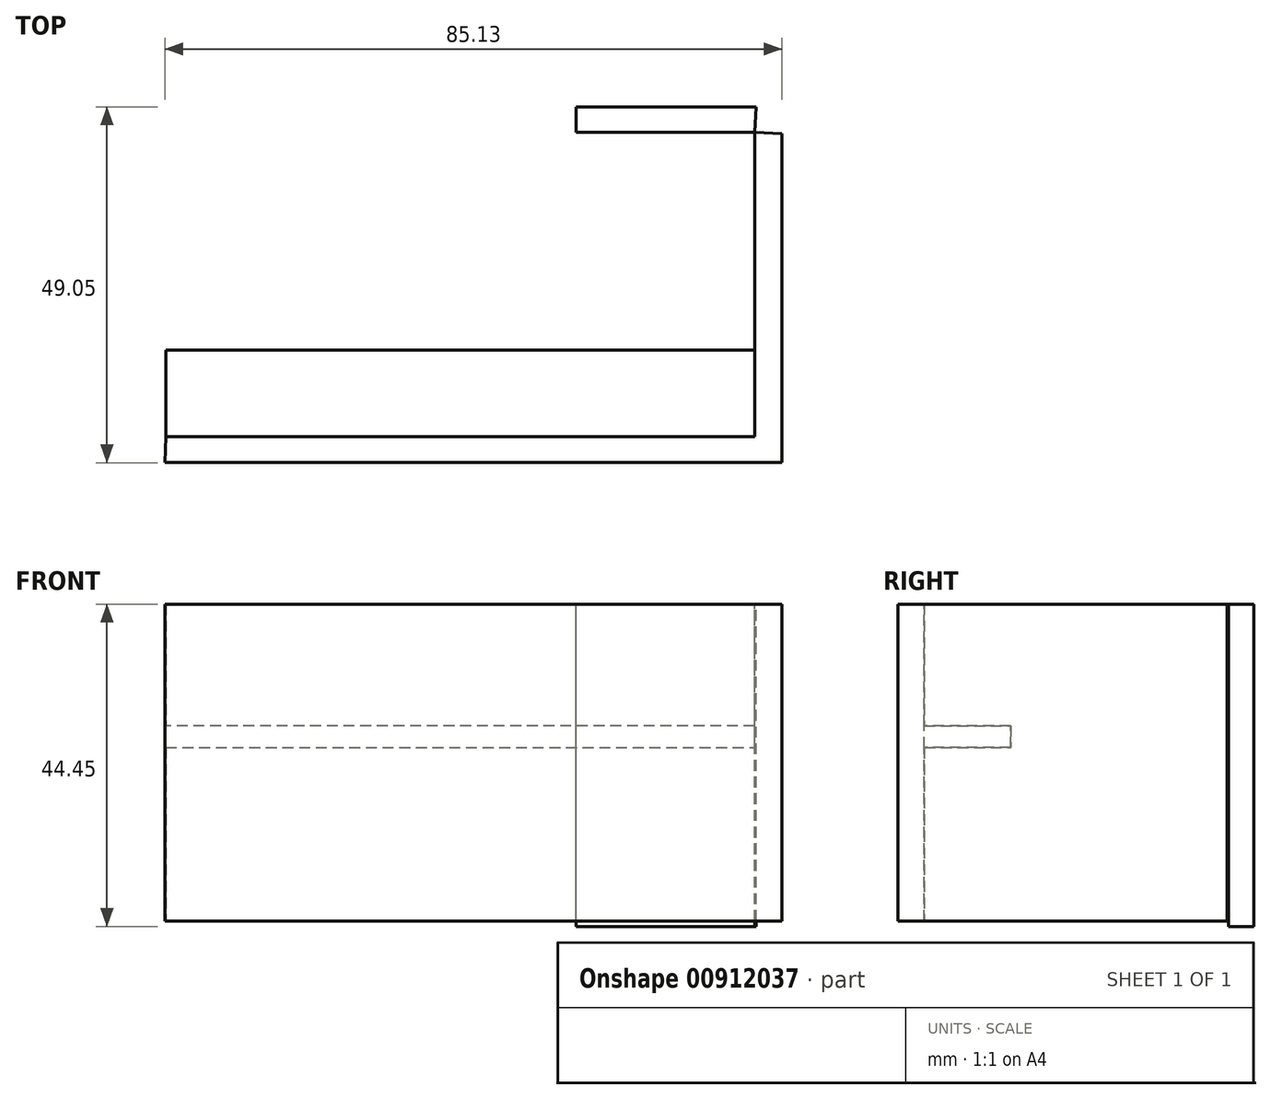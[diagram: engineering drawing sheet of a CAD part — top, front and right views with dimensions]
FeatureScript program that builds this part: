
annotation { "Feature Type Name" : "Feature", "Feature Type Description" : "" }
export const myFeature = defineFeature(function(context is Context, id is Id, definition is map)
    precondition{}
    {
        {
            var Q0;
            Q0=qCreatedBy(makeId("Top.planeOp"),FACE);
            var sketch = newSketch(context, id + "F0", { "sketchPlane" : qUnion([Q0])});
            skLineSegment(sketch, "E0", {"start": v(-39.37, -23.5) * mm, "end": v(41.83, -23.5) * mm});
            skLineSegment(sketch, "E1", {"start": v(41.83, -23.5) * mm, "end": v(41.83, 18.49) * mm});
            skLineSegment(sketch, "E2", {"start": v(41.83, 18.49) * mm, "end": v(-39.37, 18.49) * mm});
            skLineSegment(sketch, "E3", {"start": v(-39.37, 18.49) * mm, "end": v(-39.37, -23.5) * mm});
            skLineSegment(sketch, "E4", {"start": v(41.83, 10.61) * mm, "end": v(17.22, 10.61) * mm});
            skLineSegment(sketch, "E5", {"start": v(17.22, 10.61) * mm, "end": v(17.22, 18.49) * mm});
            skLineSegment(sketch, "E6", {"start": v(-39.37, 3.32) * mm, "end": v(-47.74, 3.32) * mm});
            skLineSegment(sketch, "E7", {"start": v(-47.74, 3.32) * mm, "end": v(-47.74, 29.92) * mm});
            skLineSegment(sketch, "E8", {"start": v(-47.74, 29.92) * mm, "end": v(-10, 29.92) * mm});
            skLineSegment(sketch, "E9", {"start": v(-10, 29.92) * mm, "end": v(-10, 18.49) * mm});
            skLineSegment(sketch, "E10", {"start": v(17.2, 15.15) * mm, "end": v(17.2, 21.95) * mm});
            skLineSegment(sketch, "E11", {"start": v(-10.12, 15.15) * mm, "end": v(-10, 22.18) * mm});
            skLineSegment(sketch, "E12", {"start": v(12.97, -27.73) * mm, "end": v(12.97, -18.71) * mm});
            skLineSegment(sketch, "E13", {"start": v(-9.3, -27.09) * mm, "end": v(-9.3, -18.07) * mm});
            skLineSegment(sketch, "E14", {"start": v(-39.37, -11.56) * mm, "end": v(-47.98, -11.56) * mm});
            skLineSegment(sketch, "E15", {"start": v(-47.98, -11.56) * mm, "end": v(-47.98, -22.58) * mm});
            skLineSegment(sketch, "E16", {"start": v(-39.37, -22.49) * mm, "end": v(-47.98, -22.58) * mm});
            skLineSegment(sketch, "E17", {"start": v(17.2, 21.95) * mm, "end": v(42.03, 21.95) * mm});
            skLineSegment(sketch, "E18", {"start": v(41.83, 18.49) * mm, "end": v(42.03, 21.95) * mm});
            skLineSegment(sketch, "E19", {"start": v(41.83, 18.49) * mm, "end": v(45.62, 18.27) * mm});
            skLineSegment(sketch, "E20", {"start": v(45.62, 18.27) * mm, "end": v(45.62, -27.1) * mm});
            skLineSegment(sketch, "E21", {"start": v(45.62, -27.1) * mm, "end": v(-39.51, -27.1) * mm});
            skLineSegment(sketch, "E22", {"start": v(-39.51, -27.1) * mm, "end": v(-39.37, -23.5) * mm});
            skSolve(sketch);
        }
        {
            var Q0;
            {var subQ0=sQuery(id+"F0.wireOp",EDGE,"E17");Q0=makeQuery(id+"F0.imprint","IMPRINT",FACE,{"disambiguationData":[TD([[makeQuery(id+"F0.imprint","IMPRINT",EDGE,{"derivedFrom":subQ0}),-1.0]])]});}
            extrude(context, id + "F1", {"entities" : qUnion([Q0]), "oppositeDirection" : true, "depth" : 44.45 * mm, "offsetDistance" : 25.4 * mm});
        }
        {
            var Q0;
            {var subQ0=sQuery(id+"F0.wireOp",EDGE,"E19");Q0=makeQuery(id+"F0.imprint","IMPRINT",FACE,{"disambiguationData":[TD([[makeQuery(id+"F0.imprint","IMPRINT",EDGE,{"derivedFrom":subQ0}),-1.0]])]});}
            var Q1;
            {var subQ0=sQuery(id+"F0.wireOp",EDGE,"E22");Q1=makeQuery(id+"F0.imprint","IMPRINT",FACE,{"disambiguationData":[TD([[makeQuery(id+"F0.imprint","IMPRINT",EDGE,{"derivedFrom":subQ0}),-1.0]])]});}
            extrude(context, id + "F2", {"entities" : qUnion([Q0, Q1]), "oppositeDirection" : true, "depth" : 43.69 * mm, "offsetDistance" : 25.4 * mm});
        }
        {
            var Q0;
            Q0=makeQuery(id+"F2.opExtrude","SWEPT_FACE",FACE,{"disambiguationData":[OSD([sQuery(id+"F0.wireOp",EDGE,"E0")])]});
            var sketch = newSketch(context, id + "F3", { "sketchPlane" : qUnion([Q0])});
            skLineSegment(sketch, "E23", {"start": v(39.37, -19.79) * mm, "end": v(-41.83, -19.79) * mm});
            skLineSegment(sketch, "E24", {"start": v(-41.83, -19.79) * mm, "end": v(-41.83, -16.77) * mm});
            skLineSegment(sketch, "E25", {"start": v(-41.83, -16.77) * mm, "end": v(39.37, -16.77) * mm});
            skLineSegment(sketch, "E26", {"start": v(39.37, -16.77) * mm, "end": v(39.37, -19.79) * mm});
            skSolve(sketch);
        }
        {
            var Q0;
            Q0 = qSketchRegion(id + "F3", true);
            extrude(context, id + "F4", {"entities" : qUnion([Q0]), "operationType" : NewBodyOperationType.ADD, "depth" : 11.94 * mm, "offsetDistance" : 25.4 * mm});
        }
    });
